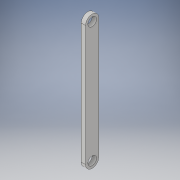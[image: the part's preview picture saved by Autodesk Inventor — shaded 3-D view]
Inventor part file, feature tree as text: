
AUTODESK INVENTOR PART (.ipt)
format: ipt  version: 2017 (Build 210142000, 142)  size: 101,376 bytes
history: native  units: in
note: dims shown in document units (in); Inventor stores cm internally (conversion verified against a paired STEP export)
features: extrude x1, sketch x1
ambient origin geometry x8: Origin, YZ Plane, XZ Plane, XY Plane, X Axis, Y Axis, Z Axis, Center Point
bodies: Solid1 (feature_tree)
feature tree (2):
  extrude  "Extrusion1"  Depth=0.77in
  sketch  "Sketch1"  dims[d0=0.5in d1=0.77in d2=7.0in d3=7.0in d4=0.5in d5=0.25in d6=0.0in]
